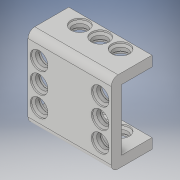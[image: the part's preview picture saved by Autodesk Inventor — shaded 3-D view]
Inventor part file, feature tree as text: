
AUTODESK INVENTOR PART (.ipt)
format: ipt  version: 2018 (Build 220112000, 112)  size: 271,872 bytes
history: native  units: in
note: dims shown in document units (in); Inventor stores cm internally (conversion verified against a paired STEP export)
features: extrude x9, sketch x9, chamfer x6, pattern_linear x3, fillet x2
ambient origin geometry x8: Origin, YZ Plane, XZ Plane, XY Plane, X Axis, Y Axis, Z Axis, Center Point
bodies: Solid1 (feature_tree)
feature tree (29):
  extrude  "Extrusion1"  Depth=0.1181in
  extrude  "Extrusion2"  Depth=0.9646in TaperAngle=0.0deg
  extrude  "Extrusion3"  Depth=0.4823in
  extrude  "Extrusion4"  Depth=0.9646in TaperAngle=0.0deg
  chamfer  "Chamfer1"  Distance=0.0394in
  chamfer  "Chamfer2"  Distance=0.0394in
  extrude  "Extrusion5"  Depth=0.0787in TaperAngle=45.0deg
  extrude  "Extrusion6"  Depth=0.0394in TaperAngle=0.0deg
  chamfer  "Chamfer3"  Distance=0.0394in
  chamfer  "Chamfer4"  Distance=0.0787in Angle=45.0deg
  pattern_linear  "Rectangular Pattern1"  Spacing1=0.0217in  [1 undecoded]
  extrude  "Extrusion7"  Depth=0.0787in
  extrude  "Extrusion8"  Depth=0.0787in
  extrude  "Extrusion9"  Depth=0.0787in
  chamfer  "Chamfer5"  Distance=0.3543in
  chamfer  "Chamfer6"  Distance=0.1614in
  pattern_linear  "Rectangular Pattern2"  Spacing1=0.3543in  [1 undecoded]
  pattern_linear  "Rectangular Pattern3"  Spacing1=0.7087in  [1 undecoded]
  fillet  "Fillet1"  Radius=0.0394in
  fillet  "Fillet2"  Radius=0.2047in
  sketch  "Sketch2"  dims[d2=0.9449in d3=0.1181in]
  sketch  "Sketch3"  dims[d4=0.4724in d5=0.9646in d6=0.0in]
  sketch  "Sketch4"  dims[d7=0.1614in d8=0.4823in]
  sketch  "Sketch5"  dims[d10=0.1181in d11=0.9646in d12=0.0in]
  sketch  "Sketch6"  dims[d13=0.2047in d14=0.0394in d15=0.0in]
  sketch  "Sketch7"  dims[d16=0.2047in d17=0.0394in d18=0.0in]
  sketch  "Sketch8"  dims[d19=0.0217in d20=0.0787in d21=45.0deg d22=0.0217in d23=0.0787in d24=45.0deg]
  sketch  "Sketch9"  dims[d25=0.2047in d26=0.0394in d27=0.0in]
  sketch  "Sketch10"  dims[d28=0.2047in d29=0.0394in d30=0.0in d31=0.0217in d32=0.0787in d33=45.0deg d34=0.0217in d35=0.0787in d36=45.0deg d37=0.7874in d39=0.2362in d40=0.7874in d42=0.2362in d44=0.4823in d45=0.3543in d46=0.1614in d47=0.3543in d49=0.7087in d50=0.0394in d51=0.0in d52=0.2047in d53=0.0394in d54=0.0in d55=0.2047in d56=0.0394in d57=0.0in d58=0.0217in d59=0.0787in d60=45.0deg d61=0.0217in d62=0.0787in d63=45.0deg d64=0.7874in d66=0.2362in d67=0.7874in d69=0.2362in d70=0.7874in d72=0.7087in d73=0.0787in d74=0.0787in]
note: 3 required parameter values undecoded (feature->parameter linkage not recoverable at this tier; creation-order binding heuristic only, values carry confidence <= 0.55)
